# Revit family: LNC4(Recovery)
name_source: partatom
category: Lighting Fixtures
revit_build: Autodesk Revit 2014 (Build: 20130308_1515(x64)
units: mm (PartAtom-declared; Revit-internal decimal feet)

## types (1)
- LNC4(Recovery)
    Apparent Load = 125 VA
    Assembly Code = D5020200
    Color Filter = 16777215
    Connector Description = Lighting Connector
    Default Elevation = 48"
    Description = Large LED Litepak
    Dimming Lamp Color Temperature Shift = <None>
    Emit Shape Visible in Rendering = No
    Emit from Rectangle Length = 8"
    Emit from Rectangle Width = 17"
    Features = • Litepak LNC4 features four different lumen packages and multiple
distributions and CCT for maximum light level and mounting height flexibility
• Capable of replacing up to 400w HID solutions at over 70% energy savings
• Easy to install and retrofit existing HID luminaires with same footprint
• Zero uplight Compact LED Architectural Wallpack
• Inverted up mounting capable
• Control capabilities offer additional energy savings options
• Ideal applications include: perimeter illumination, schools, factories,
hospitals, warehouses and retail applications
    Fixture distribution = Direct
    Housing Material = Hubbell - Light Brown
    Lamp = LED
    Load Classification = Lighting
    Manufacturer = Whiteway
    Model = LNC4
    Photometric Web File = LNC4-36L-3K-035-2-U.ies
    Power Factor = 1
    Product Documentation Link = https://hubbellcdn.com
    Product Link = https://www.hubbell.com
    Reflector Finish = Hubbell - White Glass
    Tilt Angle = -90.00°
    URL = https://www.hubbell.com
    Voltage = 120 V
    Warranty = 5 years Warranty
    Wattage Comments = 124.6
    Watts = 125 W
    Wings = Paint - Hubbell - Light Silver

## geometry (parser evidence)
native form markers: Sweep x3
no freeform markers — native parametric forms only
